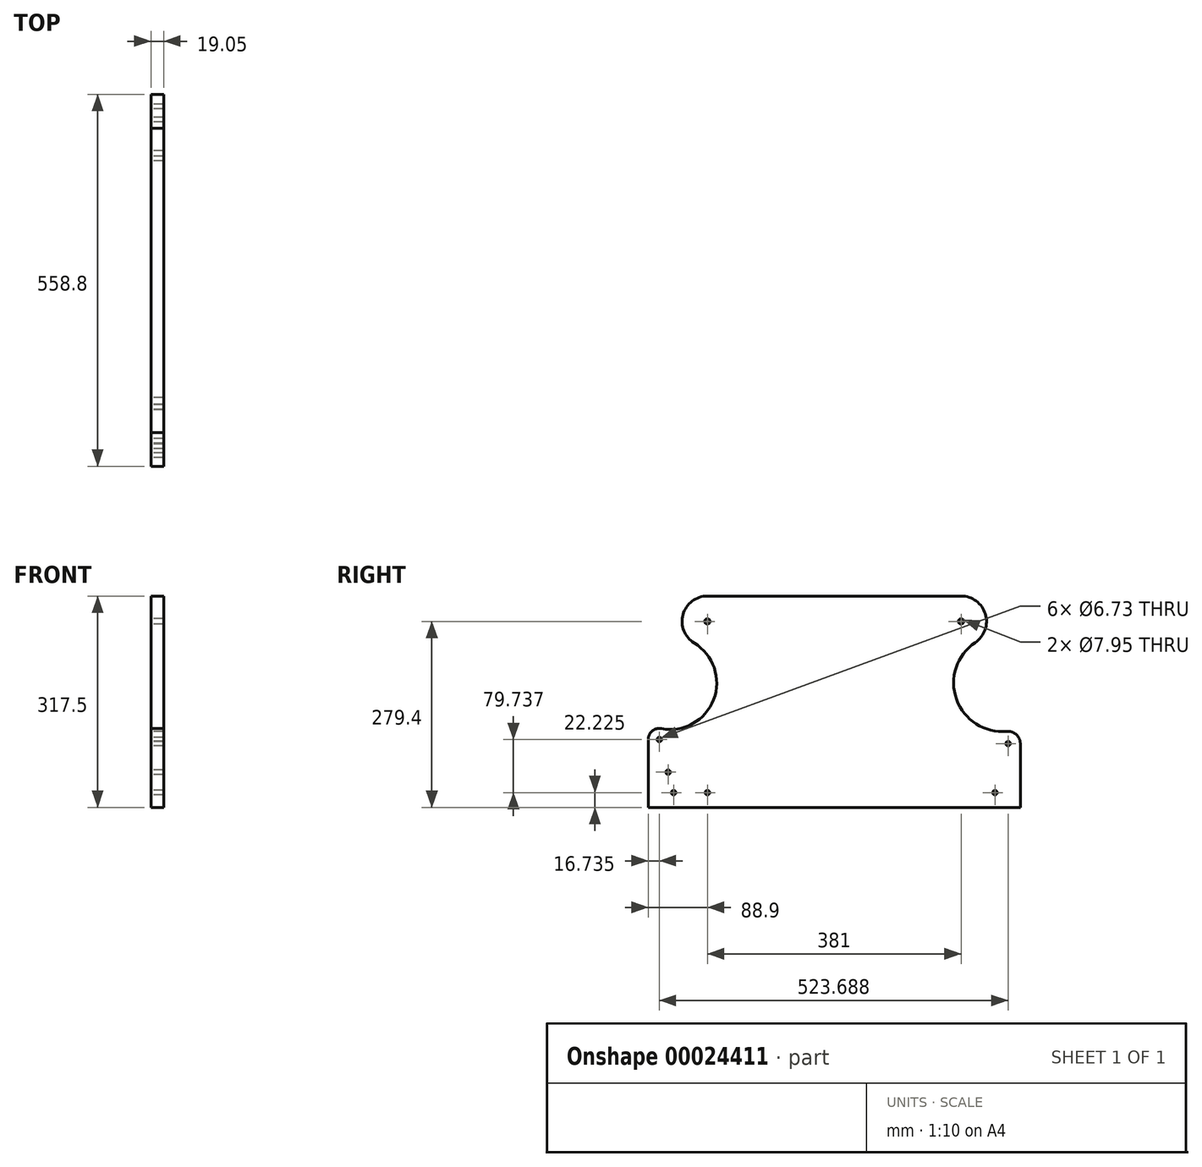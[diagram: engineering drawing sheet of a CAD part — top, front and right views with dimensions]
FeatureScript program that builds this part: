
annotation { "Feature Type Name" : "Feature", "Feature Type Description" : "" }
export const myFeature = defineFeature(function(context is Context, id is Id, definition is map)
    precondition{}
    {
        {
            var Q0;
            Q0=qCreatedBy(makeId("Right.planeOp"),FACE);
            var sketch = newSketch(context, id + "F0", { "sketchPlane" : qUnion([Q0])});
            skLineSegment(sketch, "E0.bottom", {"start": v(0, 0) * mm, "end": v(558.8, 0) * mm});
            skLineSegment(sketch, "E0.top", {"start": v(0, 317.5) * mm, "end": v(88.9, 317.5) * mm, "construction": true});
            skLineSegment(sketch, "E0.left", {"start": v(0, 0) * mm, "end": v(0, 101.96) * mm});
            skLineSegment(sketch, "E0.right", {"start": v(558.8, 0) * mm, "end": v(558.8, 95.83) * mm});
            skCircle(sketch, "E1", {"center": v(29.88, 52.9) * mm, "radius": 3.37 * mm});
            skCircle(sketch, "E2", {"center": v(16.73, 101.96) * mm, "radius": 3.37 * mm});
            skCircle(sketch, "E3", {"center": v(88.9, 279.4) * mm, "radius": 3.98 * mm});
            skCircle(sketch, "E4", {"center": v(469.9, 279.4) * mm, "radius": 3.98 * mm});
            skCircle(sketch, "E5", {"center": v(520.7, 22.22) * mm, "radius": 3.37 * mm});
            skCircle(sketch, "E6", {"center": v(540.42, 95.83) * mm, "radius": 3.37 * mm});
            skCircle(sketch, "E7", {"center": v(88.9, 22.22) * mm, "radius": 3.37 * mm});
            skCircle(sketch, "E8", {"center": v(38.1, 22.22) * mm, "radius": 3.37 * mm});
            skLineSegment(sketch, "E9", {"start": v(38.1, 22.22) * mm, "end": v(88.9, 22.22) * mm, "construction": true});
            skLineSegment(sketch, "E10", {"start": v(16.73, 101.96) * mm, "end": v(29.88, 52.9) * mm, "construction": true});
            skLineSegment(sketch, "E11", {"start": v(29.88, 52.9) * mm, "end": v(38.1, 22.22) * mm, "construction": true});
            skLineSegment(sketch, "E12", {"start": v(520.7, 22.23) * mm, "end": v(540.42, 95.83) * mm, "construction": true});
            skArc(sketch, "E13", {"start": v(88.9, 317.5) * mm, "mid": v(52.2, 289.62) * mm, "end": v(69.2, 246.78) * mm});
            skArc(sketch, "E14", {"start": v(491.12, 247.76) * mm, "mid": v(506.35, 290.5) * mm, "end": v(469.9, 317.5) * mm});
            skArc(sketch, "E15", {"start": v(19.9, 118.4) * mm, "mid": v(98.32, 161.94) * mm, "end": v(69.2, 246.78) * mm});
            skArc(sketch, "E16", {"start": v(19.9, 118.4) * mm, "mid": v(6.08, 114.87) * mm, "end": v(0, 101.96) * mm});
            skArc(sketch, "E17", {"start": v(558.8, 95.83) * mm, "mid": v(552.8, 109.42) * mm, "end": v(538.7, 114.13) * mm});
            skLineSegment(sketch, "E18", {"start": v(88.9, 317.5) * mm, "end": v(469.9, 317.5) * mm});
            skLineSegment(sketch, "E19", {"start": v(469.9, 317.5) * mm, "end": v(558.8, 317.5) * mm, "construction": true});
            skLineSegment(sketch, "E20", {"start": v(0, 101.96) * mm, "end": v(0, 317.5) * mm, "construction": true});
            skLineSegment(sketch, "E21", {"start": v(558.8, 95.83) * mm, "end": v(558.8, 317.5) * mm, "construction": true});
            skArc(sketch, "E22", {"start": v(491.12, 247.76) * mm, "mid": v(462.95, 162.44) * mm, "end": v(538.7, 114.13) * mm});
            skLineSegment(sketch, "E23", {"start": v(33.11, 186.98) * mm, "end": v(531.88, 186.98) * mm, "construction": true});
            skSolve(sketch);
        }
        {
            var Q0;
            Q0 = qSketchRegion(id + "F0", true);
            extrude(context, id + "F1", {"entities" : qUnion([Q0]), "depth" : 19.05 * mm});
        }
    });
